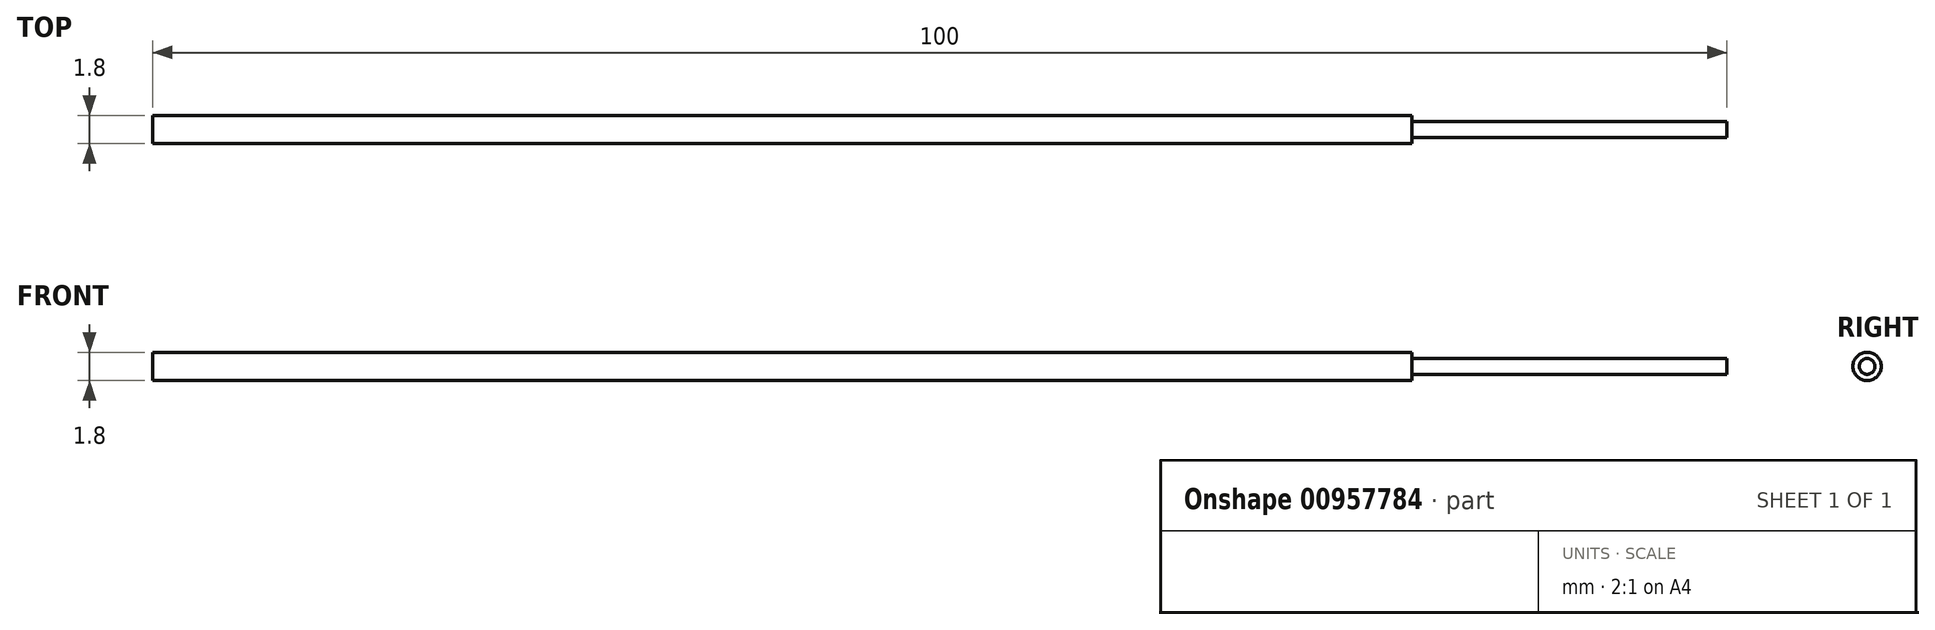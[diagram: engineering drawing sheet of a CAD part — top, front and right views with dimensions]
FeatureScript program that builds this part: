
annotation { "Feature Type Name" : "Feature", "Feature Type Description" : "" }
export const myFeature = defineFeature(function(context is Context, id is Id, definition is map)
    precondition{}
    {
        {
            var Q0;
            Q0=qCreatedBy(makeId("Front.planeOp"),FACE);
            var sketch = newSketch(context, id + "F0", { "sketchPlane" : qUnion([Q0])});
            skLineSegment(sketch, "E0", {"start": v(-80, 0) * mm, "end": v(20, 0) * mm});
            skLineSegment(sketch, "E1", {"start": v(-80, 0) * mm, "end": v(-80, 0.9) * mm});
            skLineSegment(sketch, "E2", {"start": v(-80, 0.9) * mm, "end": v(0, 0.9) * mm});
            skLineSegment(sketch, "E3", {"start": v(0, 0.9) * mm, "end": v(0, 0.5) * mm});
            skLineSegment(sketch, "E4", {"start": v(0, 0.5) * mm, "end": v(20, 0.5) * mm});
            skLineSegment(sketch, "E5", {"start": v(20, 0.5) * mm, "end": v(20, 0) * mm});
            skSolve(sketch);
        }
        {
            var Q0;
            Q0 = qSketchRegion(id + "F0", true);
            var Q1;
            Q1=sQuery(id+"F0.wireOp",EDGE,"E0");
            revolve(context, id + "F1", {"surfaceOperationType" : NewSurfaceOperationType.NEW, "entities" : qUnion([Q0]), "axis" : qUnion([Q1]), "revolveType" : RevolveType.FULL});
        }
    });
